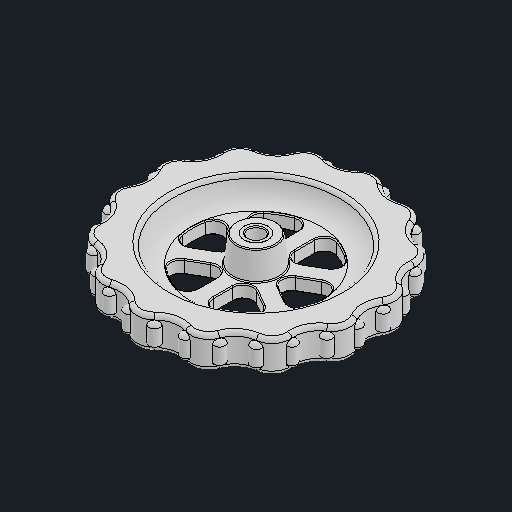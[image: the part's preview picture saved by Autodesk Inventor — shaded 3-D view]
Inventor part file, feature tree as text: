
AUTODESK INVENTOR PART (.ipt)
format: ipt  version: 2024.2 (Build 282272000, 272)  size: 904,192 bytes
history: native  units: mm
features: other x2, chamfer x1, pattern_circular x1
ambient origin geometry x8: Origin, YZ Plane, XZ Plane, XY Plane, X Axis, Y Axis, Z Axis, Center Point
bodies: Body1 (feature_tree), Body2 (feature_tree)
feature tree (4):
  other  "솔리드1"
  other  "솔리드2"
  chamfer  "Chamfer1"  [1 undecoded]
  pattern_circular  "CirPattern5"
note: 1 required parameter value undecoded (feature->parameter linkage not recoverable at this tier; creation-order binding heuristic only, values carry confidence <= 0.55)
